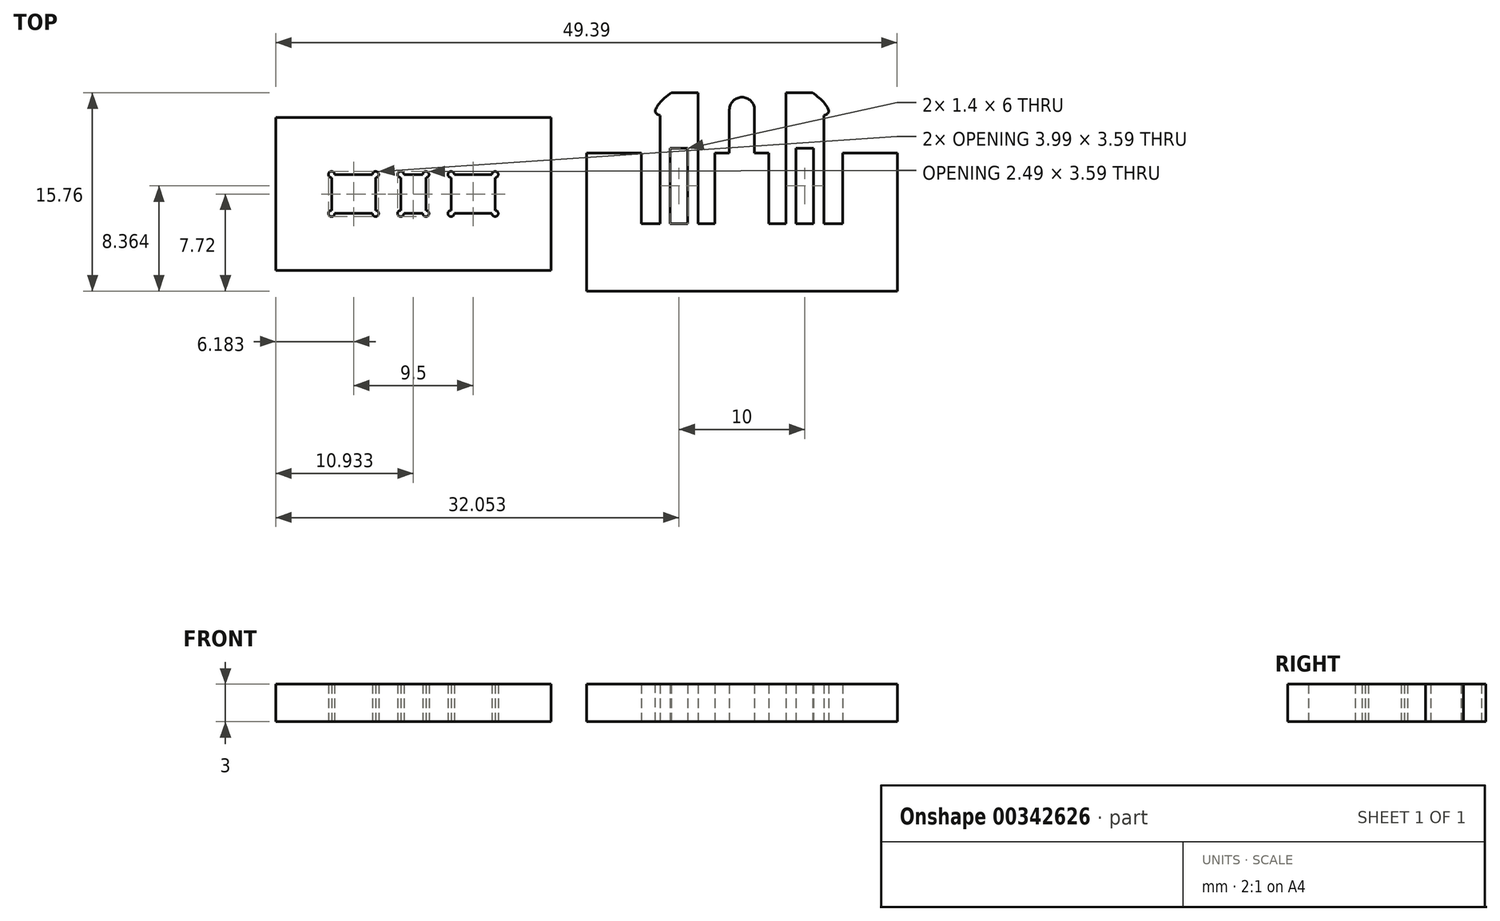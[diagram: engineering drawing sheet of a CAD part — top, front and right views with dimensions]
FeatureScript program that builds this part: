
annotation { "Feature Type Name" : "Feature", "Feature Type Description" : "" }
export const myFeature = defineFeature(function(context is Context, id is Id, definition is map)
    precondition{}
    {
        {
            var Q0;
            Q0=qCreatedBy(makeId("Top.planeOp"),FACE);
            var sketch = newSketch(context, id + "F0", { "sketchPlane" : qUnion([Q0])});
            skLineSegment(sketch, "E0", {"start": v(2.84, 3.24) * mm, "end": v(7.17, 3.24) * mm});
            skLineSegment(sketch, "E1", {"start": v(7.17, 3.24) * mm, "end": v(7.17, -2.36) * mm});
            skLineSegment(sketch, "E2", {"start": v(7.17, -2.36) * mm, "end": v(8.68, -2.36) * mm});
            skLineSegment(sketch, "E3", {"start": v(8.68, -2.36) * mm, "end": v(8.68, 6.24) * mm});
            skLineSegment(sketch, "E4", {"start": v(11.68, 8.04) * mm, "end": v(11.68, -2.36) * mm});
            skLineSegment(sketch, "E5", {"start": v(11.68, -2.36) * mm, "end": v(13.04, -2.36) * mm});
            skLineSegment(sketch, "E6", {"start": v(13.04, -2.36) * mm, "end": v(13.04, 3.24) * mm});
            skLineSegment(sketch, "E7", {"start": v(13.04, 3.24) * mm, "end": v(14.18, 3.24) * mm});
            skLineSegment(sketch, "E8", {"start": v(14.18, 3.24) * mm, "end": v(14.18, 6.7) * mm});
            skLineSegment(sketch, "E9", {"start": v(15.18, 6.7) * mm, "end": v(15.18, -8.13) * mm, "construction": true});
            skLineSegment(sketch, "E10.bottom", {"start": v(9.48, -2.36) * mm, "end": v(10.88, -2.36) * mm});
            skLineSegment(sketch, "E10.top", {"start": v(9.48, 3.64) * mm, "end": v(10.88, 3.64) * mm});
            skLineSegment(sketch, "E10.left", {"start": v(9.48, -2.36) * mm, "end": v(9.48, 3.64) * mm});
            skLineSegment(sketch, "E10.right", {"start": v(10.88, -2.36) * mm, "end": v(10.88, 3.64) * mm});
            skLineSegment(sketch, "E11", {"start": v(7.17, -2.36) * mm, "end": v(13.82, -2.36) * mm, "construction": true});
            skFitSpline(sketch, "E12", {"points": [v(8.68, 6.24) * mm, v(8.28, 6.54) * mm, v(9.57, 8.04) * mm], "startDerivative": vector(-1.97, 0.94) * mm, "endDerivative": vector(3.3, 2.07) * mm});
            skLineSegment(sketch, "E13", {"start": v(15.18, -4.9) * mm, "end": v(15.18, -4.9) * mm});
            skLineSegment(sketch, "E14", {"start": v(5.93, 8.04) * mm, "end": v(17.39, 8.04) * mm, "construction": true});
            skLineSegment(sketch, "E15", {"start": v(9.57, 8.04) * mm, "end": v(11.68, 8.04) * mm});
            skFitSpline(sketch, "E16.MirrorCS", {"points": [v(21.68, 6.24) * mm, v(22.08, 6.54) * mm, v(20.8, 8.04) * mm], "startDerivative": vector(1.97, 0.94) * mm, "endDerivative": vector(-3.3, 2.07) * mm});
            skLineSegment(sketch, "E17.MirrorCS", {"start": v(23.2, -2.36) * mm, "end": v(21.68, -2.36) * mm});
            skLineSegment(sketch, "E18.MirrorCS", {"start": v(20.88, -2.36) * mm, "end": v(19.48, -2.36) * mm});
            skLineSegment(sketch, "E19.MirrorCS", {"start": v(18.68, -2.36) * mm, "end": v(17.33, -2.36) * mm});
            skLineSegment(sketch, "E20.MirrorCS", {"start": v(23.2, -2.36) * mm, "end": v(16.54, -2.36) * mm, "construction": true});
            skLineSegment(sketch, "E21.MirrorCS", {"start": v(27.52, 3.24) * mm, "end": v(23.2, 3.24) * mm});
            skLineSegment(sketch, "E22.MirrorCS", {"start": v(19.48, -2.36) * mm, "end": v(19.48, 3.64) * mm});
            skLineSegment(sketch, "E23.MirrorCS", {"start": v(23.2, 3.24) * mm, "end": v(23.2, -2.36) * mm});
            skLineSegment(sketch, "E24.MirrorCS", {"start": v(17.33, -2.36) * mm, "end": v(17.33, 3.24) * mm});
            skLineSegment(sketch, "E25.MirrorCS", {"start": v(18.68, 8.04) * mm, "end": v(18.68, -2.36) * mm});
            skLineSegment(sketch, "E26.MirrorCS", {"start": v(21.68, -2.36) * mm, "end": v(21.68, 6.24) * mm});
            skLineSegment(sketch, "E27.MirrorCS", {"start": v(20.8, 8.04) * mm, "end": v(18.68, 8.04) * mm});
            skLineSegment(sketch, "E28.MirrorCS", {"start": v(16.18, 3.24) * mm, "end": v(16.18, 6.7) * mm});
            skLineSegment(sketch, "E29.MirrorCS", {"start": v(20.88, 3.64) * mm, "end": v(19.48, 3.64) * mm});
            skLineSegment(sketch, "E30.MirrorCS", {"start": v(17.33, 3.24) * mm, "end": v(16.18, 3.24) * mm});
            skLineSegment(sketch, "E31.MirrorCS", {"start": v(20.88, -2.36) * mm, "end": v(20.88, 3.64) * mm});
            skArc(sketch, "E32", {"start": v(14.18, 6.7) * mm, "mid": v(15.18, 7.7) * mm, "end": v(16.18, 6.7) * mm});
            skLineSegment(sketch, "E33", {"start": v(2.84, 3.24) * mm, "end": v(2.84, -7.72) * mm});
            skLineSegment(sketch, "E34", {"start": v(2.84, -7.72) * mm, "end": v(27.52, -7.72) * mm});
            skLineSegment(sketch, "E35", {"start": v(27.52, -7.72) * mm, "end": v(27.52, 3.24) * mm});
            skLineSegment(sketch, "E36.bottom", {"start": v(-21.87, 6.07) * mm, "end": v(0, 6.07) * mm});
            skLineSegment(sketch, "E36.top", {"start": v(-21.87, -6.07) * mm, "end": v(0, -6.07) * mm});
            skLineSegment(sketch, "E36.left", {"start": v(-21.87, 6.07) * mm, "end": v(-21.87, -6.07) * mm});
            skLineSegment(sketch, "E36.right", {"start": v(0, 6.07) * mm, "end": v(0, -6.07) * mm});
            skLineSegment(sketch, "E37.bottom", {"start": v(-17.44, 1.55) * mm, "end": v(-13.94, 1.55) * mm});
            skLineSegment(sketch, "E37.top", {"start": v(-17.44, -1.55) * mm, "end": v(-13.94, -1.55) * mm});
            skLineSegment(sketch, "E37.left", {"start": v(-17.44, 1.55) * mm, "end": v(-17.44, -1.55) * mm});
            skLineSegment(sketch, "E37.right", {"start": v(-13.94, 1.55) * mm, "end": v(-13.94, -1.55) * mm});
            skLineSegment(sketch, "E38.bottom", {"start": v(-11.94, 1.55) * mm, "end": v(-9.94, 1.55) * mm});
            skLineSegment(sketch, "E38.top", {"start": v(-11.94, -1.55) * mm, "end": v(-9.94, -1.55) * mm});
            skLineSegment(sketch, "E38.left", {"start": v(-11.94, 1.55) * mm, "end": v(-11.94, -1.55) * mm});
            skLineSegment(sketch, "E38.right", {"start": v(-9.94, 1.55) * mm, "end": v(-9.94, -1.55) * mm});
            skLineSegment(sketch, "E39.bottom", {"start": v(-7.94, 1.55) * mm, "end": v(-4.44, 1.55) * mm});
            skLineSegment(sketch, "E39.top", {"start": v(-7.94, -1.55) * mm, "end": v(-4.44, -1.55) * mm});
            skLineSegment(sketch, "E39.left", {"start": v(-7.94, 1.55) * mm, "end": v(-7.94, -1.55) * mm});
            skLineSegment(sketch, "E39.right", {"start": v(-4.44, 1.55) * mm, "end": v(-4.44, -1.55) * mm});
            skPoint(sketch, "E40", {"position": v(-10.94, -1.55) * mm});
            skPoint(sketch, "E41", {"position": v(-10.94, -6.07) * mm});
            skLineSegment(sketch, "E42", {"start": v(-10.94, -1.55) * mm, "end": v(-10.94, -6.07) * mm, "construction": true});
            skCircle(sketch, "E43", {"center": v(-17.44, 1.55) * mm, "radius": 0.25 * mm});
            skCircle(sketch, "E44", {"center": v(-13.94, 1.55) * mm, "radius": 0.25 * mm});
            skCircle(sketch, "E45", {"center": v(-13.94, -1.55) * mm, "radius": 0.25 * mm});
            skCircle(sketch, "E46", {"center": v(-17.44, -1.55) * mm, "radius": 0.25 * mm});
            skCircle(sketch, "E47", {"center": v(-11.94, -1.55) * mm, "radius": 0.25 * mm});
            skCircle(sketch, "E48", {"center": v(-11.94, 1.55) * mm, "radius": 0.25 * mm});
            skCircle(sketch, "E49.MirrorC", {"center": v(-4.44, -1.55) * mm, "radius": 0.25 * mm});
            skCircle(sketch, "E50.MirrorC", {"center": v(-4.44, 1.55) * mm, "radius": 0.25 * mm});
            skCircle(sketch, "E51.MirrorC", {"center": v(-7.94, 1.55) * mm, "radius": 0.25 * mm});
            skCircle(sketch, "E52.MirrorC", {"center": v(-7.94, -1.55) * mm, "radius": 0.25 * mm});
            skCircle(sketch, "E53.MirrorC", {"center": v(-9.94, -1.55) * mm, "radius": 0.25 * mm});
            skCircle(sketch, "E54.MirrorC", {"center": v(-9.94, 1.55) * mm, "radius": 0.25 * mm});
            skSolve(sketch);
        }
        {
            var Q0;
            Q0=makeQuery(id+"F0.imprint","IMPRINT",FACE,{"disambiguationData":[TD([[makeQuery(id+"F0.imprint","IMPRINT",EDGE,{"derivedFrom":sQuery(id+"F0.wireOp",EDGE,"E0")}),-1.0]])]});
            var Q1;
            Q1=makeQuery(id+"F0.imprint","IMPRINT",FACE,{"disambiguationData":[TD([[makeQuery(id+"F0.imprint","IMPRINT",EDGE,{"derivedFrom":sQuery(id+"F0.wireOp",EDGE,"E36.bottom")}),-1.0]])]});
            extrude(context, id + "F1", {"entities" : qUnion([Q0, Q1]), "depth" : 3 * mm});
        }
    });
